# Revit family: Faucet-Lavatory-KOHLER-STRAYT-K-37329T_1
name_source: partatom
category: Plumbing Fixtures
revit_build: Autodesk Revit 2017 (Build: 20160225_1515(x64)
units: mm (PartAtom-declared; Revit-internal decimal feet)

## family parameters
Cut with Voids When Loaded = No
Host = Face
OmniClass Number = 23.31.11.00
OmniClass Title = Faucets
Part Type = Normal
Room Calculation Point = No
Round Connector Dimension = Use Diameter
Shared = No

## types (4) — shared parameters
ADA Compliant = No
Assembly Code = D2010
CW Connection = Yes
Cold Water Inlet = Cold Water Inlet
Date Modified = 09/28/2021
Default Elevation = 36"
Description = Single lever bowl mixer
Drain Included = Yes
Finish = Kohler-Metal-CP-Polished_Chrome
Flow Rate = 2 GPM
HW Connection = Yes
Handle Clearance = 3 1/4"
Height = 12 5/8"
Hot Water Inlet = Hot Water Inlet
Length = 5 3/16"
Manufacturer = KOHLER Co.
Master Format 2014 = 22 41 39
Master Format 2014 Name = Residential Faucets, Supplies, and Trim
Material = Premium Metal Construction
Pressure = 45.00 psi
Product Name = STRAYT
Spout Reach = 5 3/16"
URL = http://www.kohler.com.cn
Vent Connection = No
Waste Connection = No
Waste Water Outlet = Waste Water Outlet
WaterSense Certified = No
Width = 1 13/16"

## per-type parameters (varying)
| type | Handle With Red Design | Handle With White Design | Model | Product Documentation Link | Product Page URL | Secondary Finish | Type | Without Handle Design | Without Lift rod |
| 4, CP-Polished Chrome | No | No | K-37329T-4-CP | https://files.kohler.com.cn | https://www.kohler.com.cn | Kohler-Metal-CP-Polished_Chrome | 1 | Yes | Yes |
| 4DPR, CP-Polished Chrome | Yes | No | K-37329T-4DPR-CP | https://files.kohler.com.cn | https://www.kohler.com.cn | Kohler-Plastic-Red | 2 | No | Yes |
| 4DPW, CP-Polished Chrome | No | Yes | K-37329T-4DPW-CP | https://files.kohler.com.cn | https://www.kohler.com.cn | Kohler-Plastic-0-White | 3 | No | Yes |
| B4, CP-Polished Chrome | No | No | K-37329T-B4-CP |  |  | Kohler-Metal-CP-Polished_Chrome | 4 | No | No |

## geometry (parser evidence)
native form markers: Sweep x4
no freeform markers — native parametric forms only
